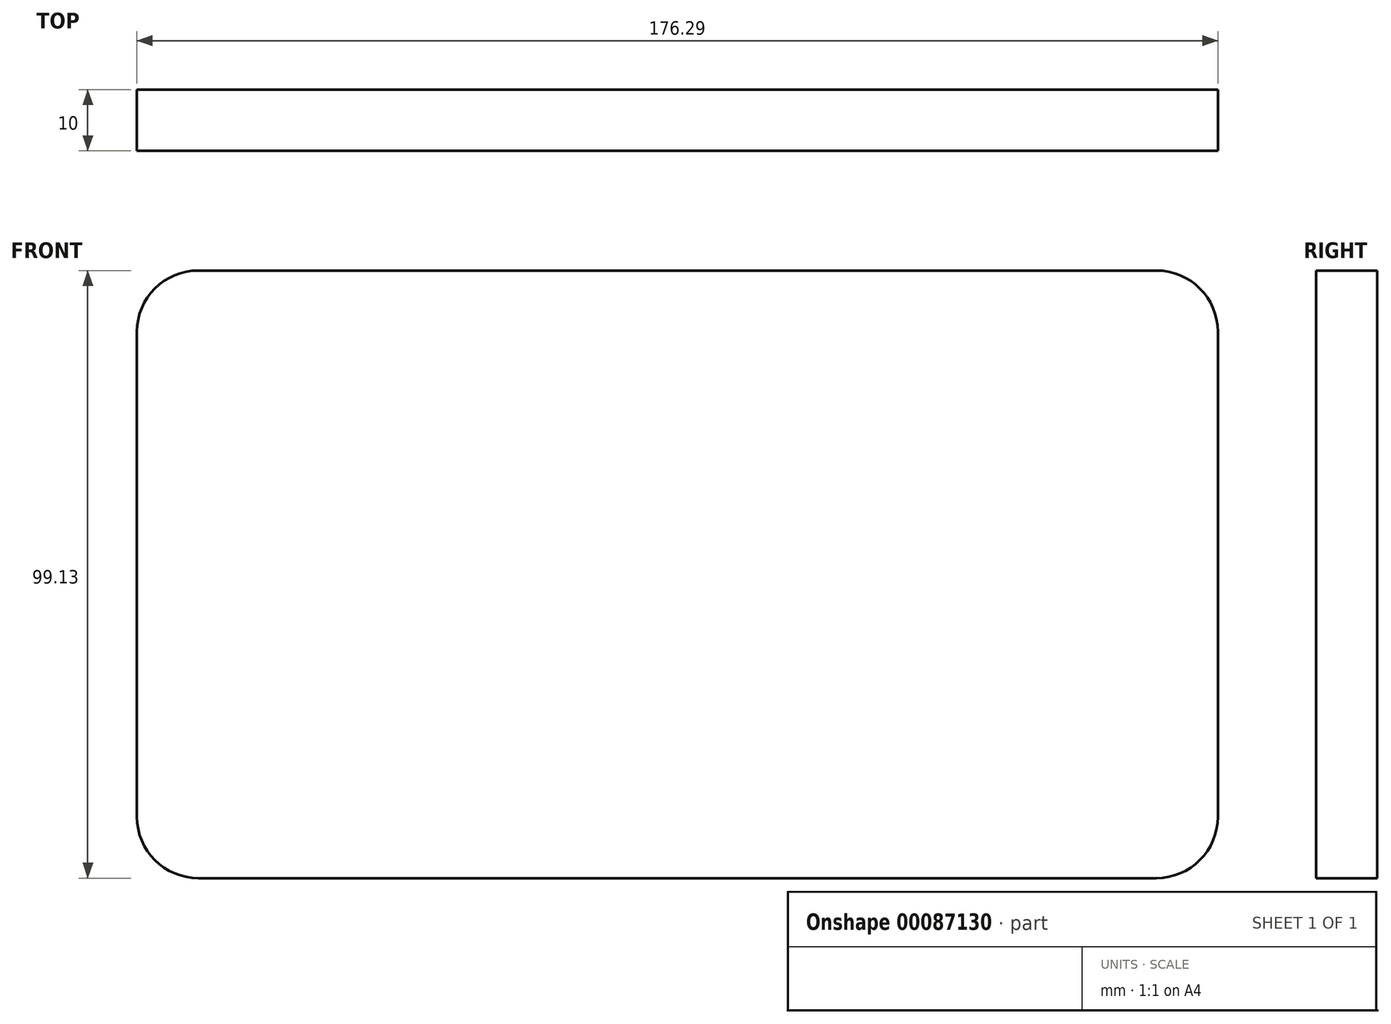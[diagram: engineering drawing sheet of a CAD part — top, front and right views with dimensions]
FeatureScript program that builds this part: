
annotation { "Feature Type Name" : "Feature", "Feature Type Description" : "" }
export const myFeature = defineFeature(function(context is Context, id is Id, definition is map)
    precondition{}
    {
        {
            var Q0;
            Q0=qCreatedBy(makeId("Front.planeOp"),FACE);
            var sketch = newSketch(context, id + "F0", { "sketchPlane" : qUnion([Q0])});
            skLineSegment(sketch, "E0.bottom", {"start": v(-69.5, 41.17) * mm, "end": v(86.79, 41.17) * mm});
            skLineSegment(sketch, "E0.top", {"start": v(-69.5, -57.96) * mm, "end": v(86.79, -57.96) * mm});
            skLineSegment(sketch, "E0.left", {"start": v(-79.5, 31.17) * mm, "end": v(-79.5, -47.96) * mm});
            skLineSegment(sketch, "E0.right", {"start": v(96.79, 31.17) * mm, "end": v(96.79, -47.96) * mm});
            skPoint(sketch, "E1.visualSharp", {"position": v(-79.5, 41.17) * mm});
            skArc(sketch, "E1.filletArc", {"start": v(-69.5, 41.17) * mm, "mid": v(-76.57, 38.24) * mm, "end": v(-79.5, 31.17) * mm});
            skPoint(sketch, "E2.visualSharp", {"position": v(96.79, 41.17) * mm});
            skArc(sketch, "E2.filletArc", {"start": v(96.79, 31.17) * mm, "mid": v(93.86, 38.24) * mm, "end": v(86.79, 41.17) * mm});
            skPoint(sketch, "E3.visualSharp", {"position": v(96.79, -57.96) * mm});
            skArc(sketch, "E3.filletArc", {"start": v(86.79, -57.96) * mm, "mid": v(93.86, -55.03) * mm, "end": v(96.79, -47.96) * mm});
            skPoint(sketch, "E4.visualSharp", {"position": v(-79.5, -57.96) * mm});
            skArc(sketch, "E4.filletArc", {"start": v(-79.5, -47.96) * mm, "mid": v(-76.57, -55.03) * mm, "end": v(-69.5, -57.96) * mm});
            skSolve(sketch);
        }
        {
            var Q0;
            Q0 = qSketchRegion(id + "F0", true);
            extrude(context, id + "F1", {"entities" : qUnion([Q0]), "depth" : 10 * mm});
        }
    });
